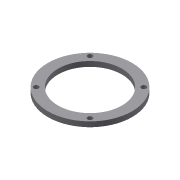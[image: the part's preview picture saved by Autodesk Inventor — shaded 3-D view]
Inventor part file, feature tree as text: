
AUTODESK INVENTOR PART (.ipt)
format: ipt  version: 2013 (Build 170138000, 138)  size: 87,552 bytes
history: native  units: in
note: dims shown in document units (in); Inventor stores cm internally (conversion verified against a paired STEP export)
features: sketch x2, extrude x1, hole x1
ambient origin geometry x8: Origin, YZ Plane, XZ Plane, XY Plane, X Axis, Y Axis, Z Axis, Center Point
bodies: Solid1 (feature_tree)
feature tree (4):
  extrude  "Extrusion1"  Depth=1.9685in
  hole  "Hole2"  [1 undecoded]
  sketch  "Sketch1"  dims[d0=1.4961in d1=1.9685in]
  sketch  "Sketch4"  dims[d2=0.1181in d3=0.0in d13=1.2598in d14=1.2598in d15=0.1142in d16=0.2362in d17=0.2165in d18=0.1969in d19=90.0deg d20=0.315in d21=0.8108in]
note: 1 required parameter value undecoded (feature->parameter linkage not recoverable at this tier; creation-order binding heuristic only, values carry confidence <= 0.55)
